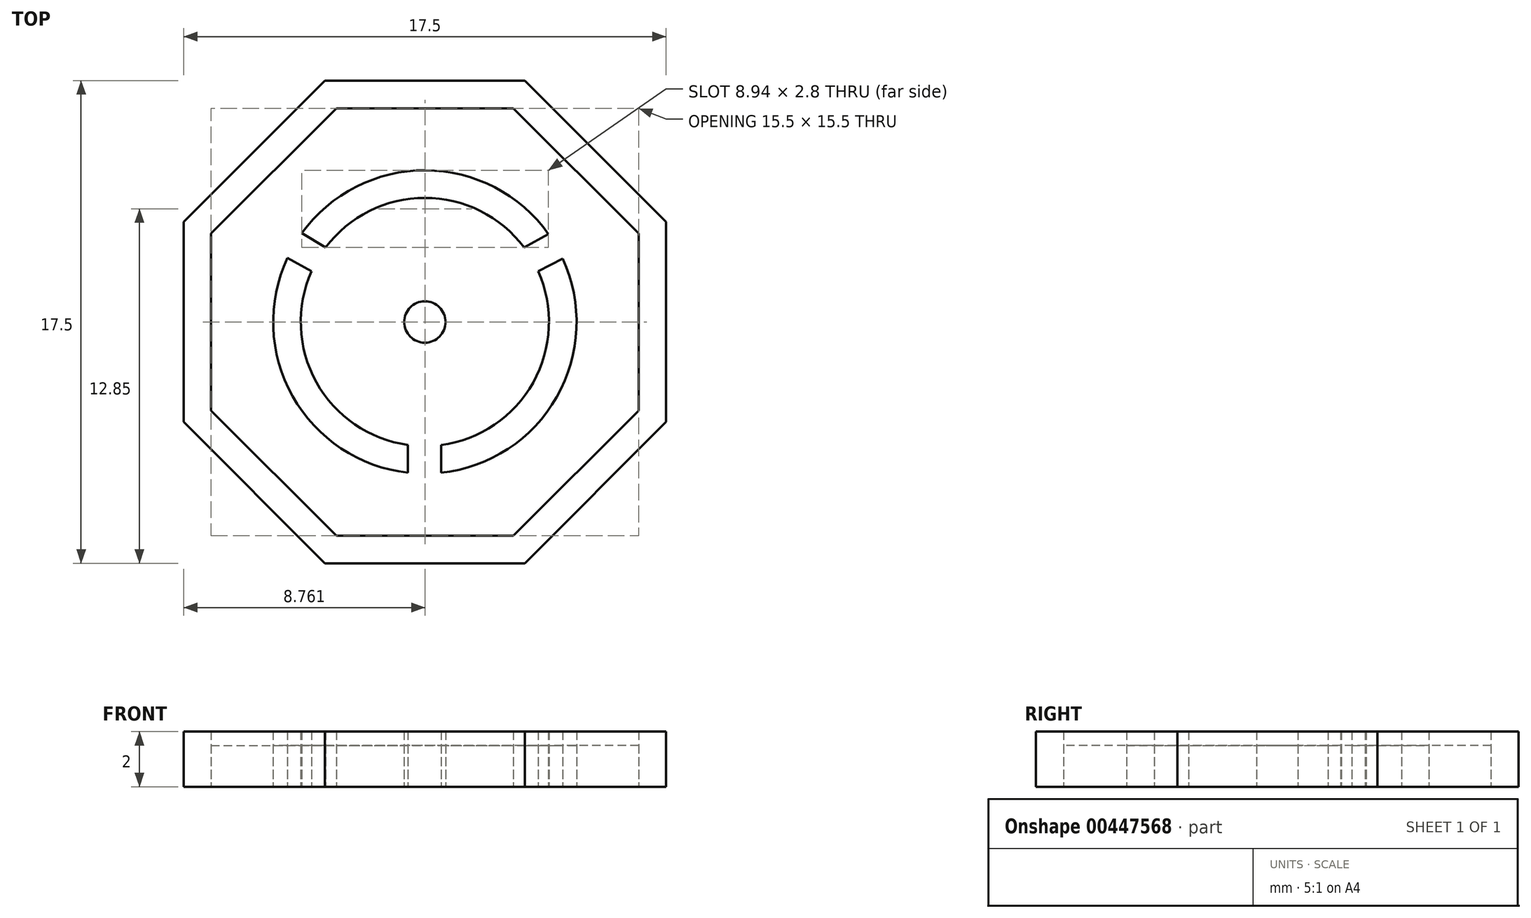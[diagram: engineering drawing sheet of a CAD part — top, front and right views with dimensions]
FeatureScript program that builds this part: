
annotation { "Feature Type Name" : "Feature", "Feature Type Description" : "" }
export const myFeature = defineFeature(function(context is Context, id is Id, definition is map)
    precondition{}
    {
        {
            var Q0;
            Q0=qCreatedBy(makeId("Top.planeOp"),FACE);
            var sketch = newSketch(context, id + "F0", { "sketchPlane" : qUnion([Q0])});
            skCircle(sketch, "E0", {"center": v(0, 0) * mm, "radius": 0.75 * mm});
            skArc(sketch, "E1", {"start": v(0.59, -4.46) * mm, "mid": v(3.93, -2.2) * mm, "end": v(4.1, 1.84) * mm});
            skArc(sketch, "E2.trimOffspring", {"start": v(-4.1, 1.84) * mm, "mid": v(-3.93, -2.18) * mm, "end": v(-0.61, -4.46) * mm});
            skArc(sketch, "E3.trimOffspring", {"start": v(3.6, 2.7) * mm, "mid": v(0, 4.5) * mm, "end": v(-3.6, 2.7) * mm});
            skArc(sketch, "E4", {"start": v(-4.98, 2.33) * mm, "mid": v(-4.8, -2.7) * mm, "end": v(-0.61, -5.47) * mm});
            skLineSegment(sketch, "E5", {"start": v(-4.1, 1.84) * mm, "end": v(-4.98, 2.33) * mm});
            skLineSegment(sketch, "E6", {"start": v(-3.6, 2.7) * mm, "end": v(-4.46, 3.22) * mm});
            skLineSegment(sketch, "E7", {"start": v(3.6, 2.7) * mm, "end": v(4.48, 3.19) * mm});
            skLineSegment(sketch, "E8", {"start": v(4.1, 1.84) * mm, "end": v(5, 2.3) * mm});
            skLineSegment(sketch, "E9", {"start": v(-0.61, -4.46) * mm, "end": v(-0.61, -5.47) * mm});
            skLineSegment(sketch, "E10", {"start": v(0.59, -4.46) * mm, "end": v(0.59, -5.47) * mm});
            skArc(sketch, "E11.trimOffspring", {"start": v(4.48, 3.19) * mm, "mid": v(0.02, 5.5) * mm, "end": v(-4.46, 3.22) * mm});
            skArc(sketch, "E12.trimOffspring", {"start": v(0.59, -5.47) * mm, "mid": v(4.78, -2.72) * mm, "end": v(5, 2.3) * mm});
            skCircle(sketch, "E13.cCircle", {"center": v(0, 0) * mm, "radius": 8.75 * mm, "construction": true});
            skLineSegment(sketch, "E13.0", {"start": v(8.75, -3.62) * mm, "end": v(3.62, -8.75) * mm});
            skLineSegment(sketch, "E13.1", {"start": v(3.62, -8.75) * mm, "end": v(-3.62, -8.75) * mm});
            skLineSegment(sketch, "E13.2", {"start": v(-3.62, -8.75) * mm, "end": v(-8.75, -3.62) * mm});
            skLineSegment(sketch, "E13.3", {"start": v(-8.75, -3.62) * mm, "end": v(-8.75, 3.62) * mm});
            skLineSegment(sketch, "E13.4", {"start": v(-8.75, 3.62) * mm, "end": v(-3.62, 8.75) * mm});
            skLineSegment(sketch, "E13.5", {"start": v(-3.62, 8.75) * mm, "end": v(3.62, 8.75) * mm});
            skLineSegment(sketch, "E13.6", {"start": v(3.62, 8.75) * mm, "end": v(8.75, 3.62) * mm});
            skLineSegment(sketch, "E13.7", {"start": v(8.75, 3.62) * mm, "end": v(8.75, -3.62) * mm});
            skPoint(sketch, "E13.0.midPoint", {"position": v(6.19, -6.19) * mm});
            skCircle(sketch, "E14.cCircle", {"center": v(0, 0) * mm, "radius": 7.75 * mm, "construction": true});
            skLineSegment(sketch, "E14.0", {"start": v(7.75, -3.21) * mm, "end": v(3.21, -7.75) * mm});
            skLineSegment(sketch, "E14.1", {"start": v(3.21, -7.75) * mm, "end": v(-3.21, -7.75) * mm});
            skLineSegment(sketch, "E14.2", {"start": v(-3.21, -7.75) * mm, "end": v(-7.75, -3.21) * mm});
            skLineSegment(sketch, "E14.3", {"start": v(-7.75, -3.21) * mm, "end": v(-7.75, 3.21) * mm});
            skLineSegment(sketch, "E14.4", {"start": v(-7.75, 3.21) * mm, "end": v(-3.21, 7.75) * mm});
            skLineSegment(sketch, "E14.5", {"start": v(-3.21, 7.75) * mm, "end": v(3.21, 7.75) * mm});
            skLineSegment(sketch, "E14.6", {"start": v(3.21, 7.75) * mm, "end": v(7.75, 3.21) * mm});
            skLineSegment(sketch, "E14.7", {"start": v(7.75, 3.21) * mm, "end": v(7.75, -3.21) * mm});
            skPoint(sketch, "E14.0.midPoint", {"position": v(5.48, -5.48) * mm});
            skSolve(sketch);
        }
        {
            var Q0;
            Q0=makeQuery(id+"F0.imprint","IMPRINT",FACE,{"disambiguationData":[TD([[makeQuery(id+"F0.imprint","IMPRINT",EDGE,{"derivedFrom":sQuery(id+"F0.wireOp",EDGE,"E13.0")}),-1.0]])]});
            var Q1;
            Q1=makeQuery(id+"F0.imprint","IMPRINT",FACE,{"disambiguationData":[TD([[makeQuery(id+"F0.imprint","IMPRINT",EDGE,{"derivedFrom":sQuery(id+"F0.wireOp",EDGE,"E3.trimOffspring")}),-1.0]])]});
            var Q2;
            Q2=makeQuery(id+"F0.imprint","IMPRINT",FACE,{"disambiguationData":[TD([[makeQuery(id+"F0.imprint","IMPRINT",EDGE,{"derivedFrom":sQuery(id+"F0.wireOp",EDGE,"E2.trimOffspring")}),-1.0]])]});
            var Q3;
            Q3=makeQuery(id+"F0.imprint","IMPRINT",FACE,{"disambiguationData":[TD([[makeQuery(id+"F0.imprint","IMPRINT",EDGE,{"derivedFrom":sQuery(id+"F0.wireOp",EDGE,"E1")}),-1.0]])]});
            var Q4;
            Q4=makeQuery(id+"F0.imprint","IMPRINT",FACE,{"disambiguationData":[TD([[makeQuery(id+"F0.imprint","IMPRINT",EDGE,{"derivedFrom":sQuery(id+"F0.wireOp",EDGE,"E0")}),1.0]])]});
            extrude(context, id + "F1", {"entities" : qUnion([Q0, Q1, Q2, Q3, Q4]), "depth" : 2 * mm});
        }
        {
            var Q0;
            Q0=makeQuery(id+"F0.imprint","IMPRINT",FACE,{"disambiguationData":[TD([[makeQuery(id+"F0.imprint","IMPRINT",EDGE,{"derivedFrom":sQuery(id+"F0.wireOp",EDGE,"E0")}),-1.0]])]});
            extrude(context, id + "F2", {"entities" : qUnion([Q0]), "depth" : 1.5 * mm});
        }
    });
